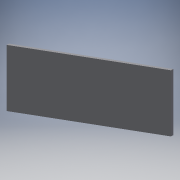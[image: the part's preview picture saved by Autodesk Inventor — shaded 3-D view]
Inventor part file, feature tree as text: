
AUTODESK INVENTOR PART (.ipt)
format: ipt  version: 2018.3 (Build 223284000, 284)  size: 4,960,256 bytes
history: native  units: mm
features: extrude x3, sketch x3, pattern_linear x2
ambient origin geometry x8: Origin, YZ Plane, XZ Plane, XY Plane, X Axis, Y Axis, Z Axis, Center Point
bodies: Solid1 (feature_tree)
feature tree (8):
  extrude  "Extrusion1"  Depth=2.0mm
  extrude  "Extrusion2"  Depth=3.0mm
  extrude  "Extrusion3"  Depth=1.0mm
  pattern_linear  "Rectangular Pattern1"  Spacing1=1.0mm  [1 undecoded]
  pattern_linear  "Rectangular Pattern2"  Spacing1=0.2mm  [1 undecoded]
  sketch  "Sketch1"  dims[d0=105.0mm d1=2.0mm]
  sketch  "Sketch2"  dims[d2=50.0mm d3=0.0mm d4=3.0mm]
  sketch  "Sketch3"  dims[d5=3.0mm d27=1.0mm d40=1.0mm d41=0.2mm d42=0.4mm d43=0.2mm d44=0.4mm d45=0.1mm d46=0.0mm d47=0.03mm d48=0.02mm d49=0.001mm d50=0.0mm d51=140.0mm d53=3.5mm d54=300.0mm d56=3.45mm]
note: 2 required parameter values undecoded (feature->parameter linkage not recoverable at this tier; creation-order binding heuristic only, values carry confidence <= 0.55)
